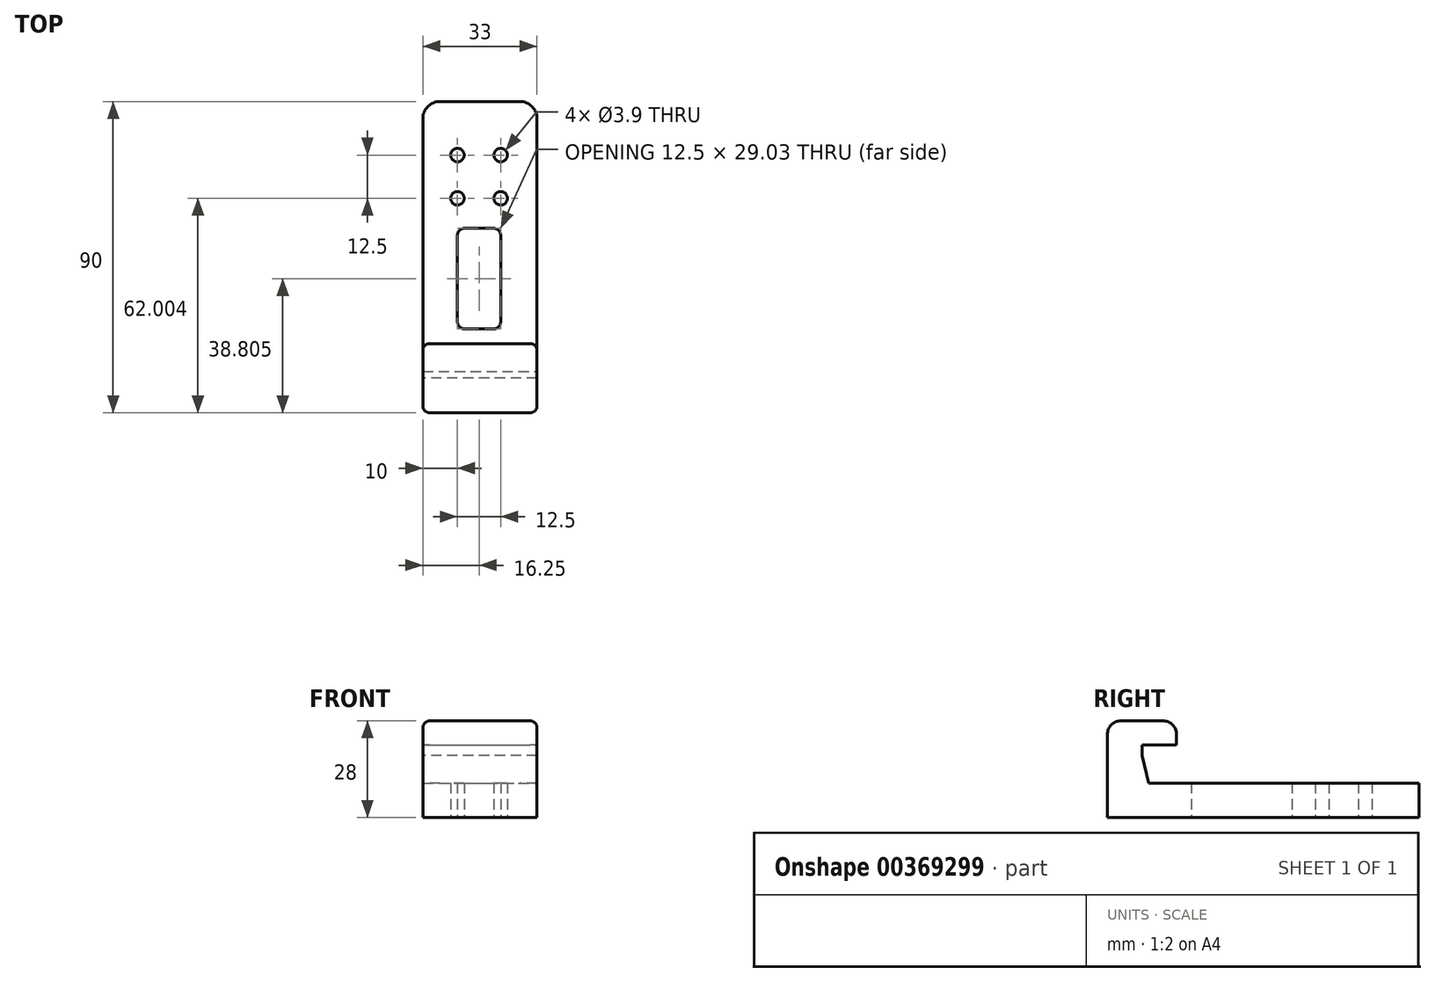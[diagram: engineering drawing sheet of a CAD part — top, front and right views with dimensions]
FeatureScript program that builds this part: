
annotation { "Feature Type Name" : "Feature", "Feature Type Description" : "" }
export const myFeature = defineFeature(function(context is Context, id is Id, definition is map)
    precondition{}
    {
        {
            var Q0;
            Q0=qCreatedBy(makeId("Top.planeOp"),FACE);
            var sketch = newSketch(context, id + "F0", { "sketchPlane" : qUnion([Q0])});
            skLineSegment(sketch, "E0.bottom", {"start": v(-65.21, 48.07) * mm, "end": v(-32.21, 48.07) * mm});
            skLineSegment(sketch, "E0.top", {"start": v(-65.21, -41.93) * mm, "end": v(-32.21, -41.93) * mm});
            skLineSegment(sketch, "E0.left", {"start": v(-65.21, 48.07) * mm, "end": v(-65.21, -41.93) * mm});
            skLineSegment(sketch, "E0.right", {"start": v(-32.21, 48.07) * mm, "end": v(-32.21, -41.93) * mm});
            skLineSegment(sketch, "E1", {"start": v(-65.21, -31.93) * mm, "end": v(-32.21, -31.93) * mm});
            skLineSegment(sketch, "E2", {"start": v(-65.21, -21.93) * mm, "end": v(-32.21, -21.93) * mm});
            skLineSegment(sketch, "E3", {"start": v(-55.21, 48.07) * mm, "end": v(-55.21, -21.93) * mm, "construction": true});
            skLineSegment(sketch, "E4", {"start": v(-42.71, 48.07) * mm, "end": v(-42.71, -21.93) * mm, "construction": true});
            skLineSegment(sketch, "E5", {"start": v(-65.21, 32.57) * mm, "end": v(-32.21, 32.57) * mm, "construction": true});
            skLineSegment(sketch, "E6", {"start": v(-65.21, 20.07) * mm, "end": v(-32.21, 20.07) * mm, "construction": true});
            skCircle(sketch, "E7", {"center": v(-55.21, 32.57) * mm, "radius": 1.95 * mm});
            skCircle(sketch, "E8", {"center": v(-42.71, 20.07) * mm, "radius": 1.95 * mm});
            skCircle(sketch, "E9", {"center": v(-42.71, 32.57) * mm, "radius": 1.95 * mm});
            skCircle(sketch, "E10", {"center": v(-55.21, 20.07) * mm, "radius": 1.95 * mm});
            skLineSegment(sketch, "E11.bottom", {"start": v(-55.21, 11.39) * mm, "end": v(-42.71, 11.39) * mm});
            skLineSegment(sketch, "E11.top", {"start": v(-55.21, -17.64) * mm, "end": v(-42.71, -17.64) * mm});
            skLineSegment(sketch, "E11.left", {"start": v(-55.21, 11.39) * mm, "end": v(-55.21, -17.64) * mm});
            skLineSegment(sketch, "E11.right", {"start": v(-42.71, 11.39) * mm, "end": v(-42.71, -17.64) * mm});
            skSolve(sketch);
        }
        {
            var Q0;
            {var subQ0=sQuery(id+"F0.wireOp",EDGE,"E0.bottom");Q0=makeQuery(id+"F0.imprint","IMPRINT",FACE,{"disambiguationData":[TD([[makeQuery(id+"F0.imprint","IMPRINT",EDGE,{"derivedFrom":subQ0}),-1.0]])]});}
            var Q1;
            {var subQ0=sQuery(id+"F0.wireOp",EDGE,"E1");Q1=makeQuery(id+"F0.imprint","IMPRINT",FACE,{"disambiguationData":[TD([[makeQuery(id+"F0.imprint","IMPRINT",EDGE,{"derivedFrom":subQ0}),1.0]])]});}
            var Q2;
            {var subQ0=sQuery(id+"F0.wireOp",EDGE,"E0.top");Q2=makeQuery(id+"F0.imprint","IMPRINT",FACE,{"disambiguationData":[TD([[makeQuery(id+"F0.imprint","IMPRINT",EDGE,{"derivedFrom":subQ0}),1.0]])]});}
            extrude(context, id + "F1", {"entities" : qUnion([Q0, Q1, Q2]), "depth" : 10 * mm});
        }
        {
            var Q0;
            {var subQ0=sQuery(id+"F0.wireOp",EDGE,"E1");Q0=makeQuery(id+"F0.imprint","IMPRINT",FACE,{"disambiguationData":[TD([[makeQuery(id+"F0.imprint","IMPRINT",EDGE,{"derivedFrom":subQ0}),1.0]])]});}
            var Q1;
            {var subQ0=sQuery(id+"F0.wireOp",EDGE,"E0.top");Q1=makeQuery(id+"F0.imprint","IMPRINT",FACE,{"disambiguationData":[TD([[makeQuery(id+"F0.imprint","IMPRINT",EDGE,{"derivedFrom":subQ0}),1.0]])]});}
            extrude(context, id + "F2", {"entities" : qUnion([Q0, Q1]), "operationType" : NewBodyOperationType.ADD, "depth" : 28 * mm});
        }
        {
            var Q0;
            {var subQ0=sQuery(id+"F0.wireOp",EDGE,"E1");Q0=makeQuery(id+"F0.imprint","IMPRINT",FACE,{"disambiguationData":[TD([[makeQuery(id+"F0.imprint","IMPRINT",EDGE,{"derivedFrom":subQ0}),1.0]])]});}
            extrude(context, id + "F3", {"entities" : qUnion([Q0]), "operationType" : NewBodyOperationType.REMOVE, "depth" : 21 * mm, "hasSecondDirection" : true, "secondDirectionOppositeDirection" : false, "secondDirectionDepth" : 10 * mm});
        }
        {
            var Q0;
            Q0=makeQuery(id+"F3.boolean.opBoolean","COPY",EDGE,{"derivedFrom":makeQuery(id+"F3.opExtrude","CAP_EDGE",EDGE,{"disambiguationData":[OSD([sQuery(id+"F0.wireOp",EDGE,"E1")])],"isStart":true})});
            chamfer(context, id + "F4", {"entities" : qUnion([Q0]), "chamferType" : ChamferType.TWO_OFFSETS, "width1" : 2 * mm, "oppositeDirection" : false, "width2" : 8 * mm, "tangentPropagation" : true});
        }
        {
            var Q0;
            Q0=makeQuery(id+"F2.opExtrude","CAP_EDGE",EDGE,{"disambiguationData":[OSD([sQuery(id+"F0.wireOp",EDGE,"E2")])],"isStart":false});
            var Q1;
            Q1=makeQuery(id+"F2.opExtrude","CAP_EDGE",EDGE,{"disambiguationData":[OSD([sQuery(id+"F0.wireOp",EDGE,"E0.top")])],"isStart":false});
            fillet(context, id + "F5", {"entities" : qUnion([Q0, Q1]), "radius" : 4 * mm, "tangentPropagation" : true, "allowEdgeOverflow" : false});
        }
        {
            var Q0;
            Q0=makeQuery(id+"F1.opExtrude","SWEPT_EDGE",EDGE,{"disambiguationData":[OSD([sQuery(id+"F0.wireOp",EDGE,"E0.bottom"),sQuery(id+"F0.wireOp",EDGE,"E0.left")])]});
            var Q1;
            Q1=makeQuery(id+"F1.opExtrude","SWEPT_EDGE",EDGE,{"disambiguationData":[OSD([sQuery(id+"F0.wireOp",EDGE,"E0.bottom"),sQuery(id+"F0.wireOp",EDGE,"E0.right")])]});
            fillet(context, id + "F6", {"entities" : qUnion([Q0, Q1]), "radius" : 5 * mm, "tangentPropagation" : true, "allowEdgeOverflow" : false});
        }
        {
            var Q0;
            Q0=makeQuery(id+"F1.opExtrude","SWEPT_EDGE",EDGE,{"disambiguationData":[OSD([sQuery(id+"F0.wireOp",EDGE,"E11.bottom"),sQuery(id+"F0.wireOp",EDGE,"E11.right")])]});
            var Q1;
            Q1=makeQuery(id+"F1.opExtrude","SWEPT_EDGE",EDGE,{"disambiguationData":[OSD([sQuery(id+"F0.wireOp",EDGE,"E11.bottom"),sQuery(id+"F0.wireOp",EDGE,"E11.left")])]});
            var Q2;
            Q2=makeQuery(id+"F1.opExtrude","SWEPT_EDGE",EDGE,{"disambiguationData":[OSD([sQuery(id+"F0.wireOp",EDGE,"E11.top"),sQuery(id+"F0.wireOp",EDGE,"E11.left")])]});
            var Q3;
            Q3=makeQuery(id+"F1.opExtrude","SWEPT_EDGE",EDGE,{"disambiguationData":[OSD([sQuery(id+"F0.wireOp",EDGE,"E11.top"),sQuery(id+"F0.wireOp",EDGE,"E11.right")])]});
            fillet(context, id + "F7", {"entities" : qUnion([Q0, Q1, Q2, Q3]), "radius" : 2 * mm, "tangentPropagation" : true, "allowEdgeOverflow" : false});
        }
        {
            var Q0;
            Q0=makeQuery(id+"F2.opExtrude","CAP_EDGE",EDGE,{"disambiguationData":[OSD([sQuery(id+"F0.wireOp",EDGE,"E0.left")])],"isStart":false});
            var Q1;
            Q1=makeQuery(id+"F2.opExtrude","CAP_EDGE",EDGE,{"disambiguationData":[OSD([sQuery(id+"F0.wireOp",EDGE,"E0.right")])],"isStart":false});
            fillet(context, id + "F8", {"entities" : qUnion([Q0, Q1]), "radius" : 2 * mm, "tangentPropagation" : true, "allowEdgeOverflow" : false});
        }
    });
